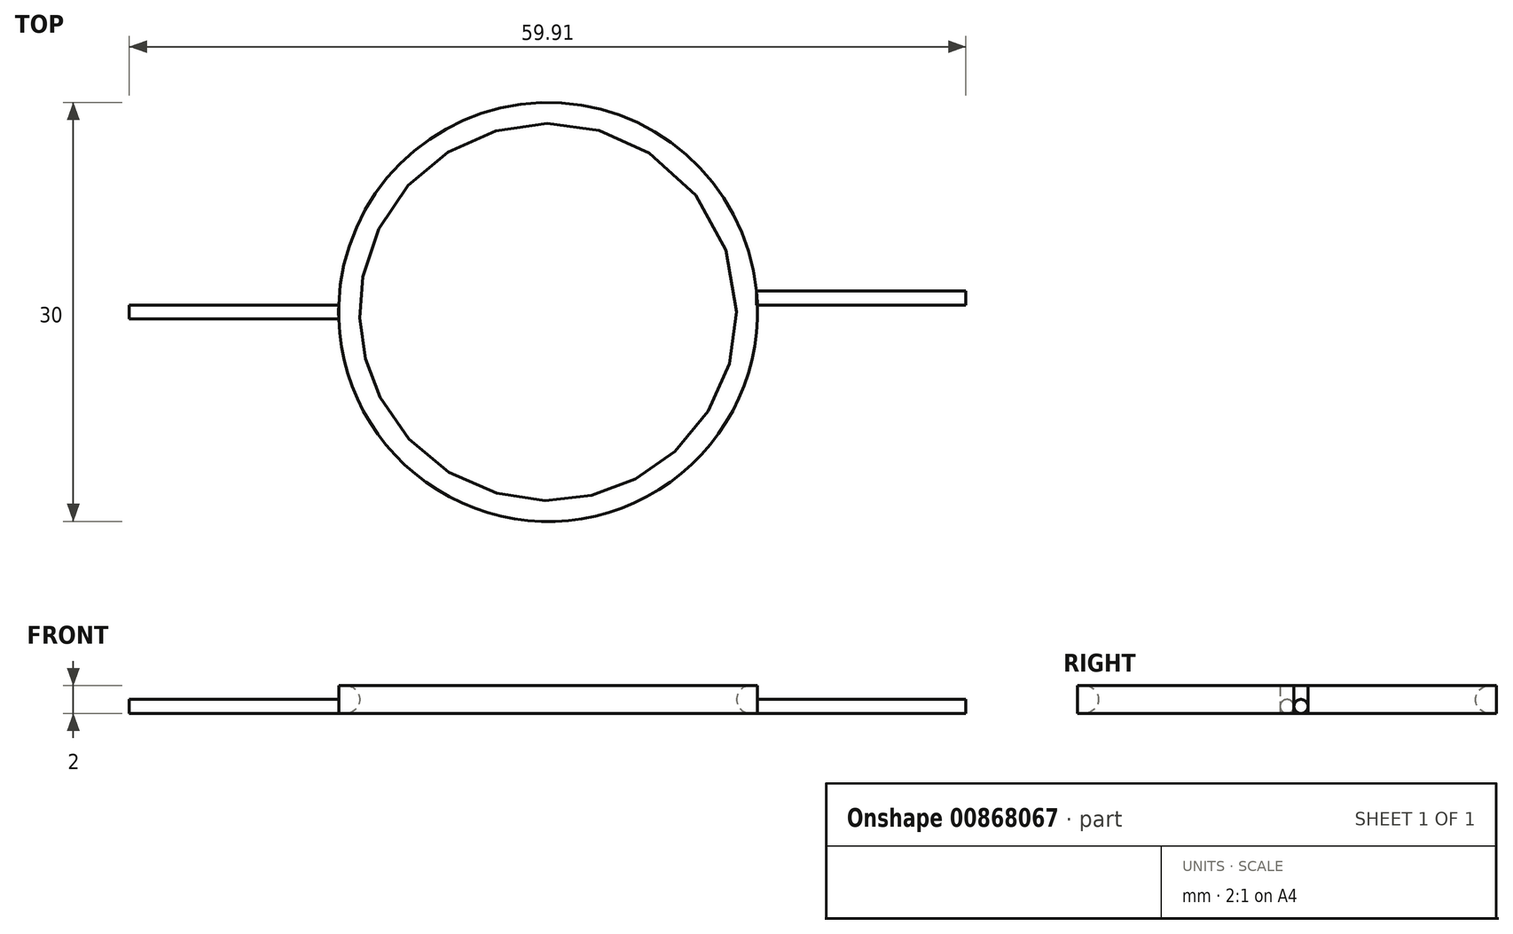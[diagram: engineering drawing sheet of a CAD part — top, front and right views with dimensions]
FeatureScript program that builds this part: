
annotation { "Feature Type Name" : "Feature", "Feature Type Description" : "" }
export const myFeature = defineFeature(function(context is Context, id is Id, definition is map)
    precondition{}
    {
        {
            var Q0;
            Q0=qCreatedBy(makeId("Top.planeOp"),FACE);
            var sketch = newSketch(context, id + "F0", { "sketchPlane" : qUnion([Q0])});
            skCircle(sketch, "E0", {"center": v(0, 0) * mm, "radius": 15 * mm});
            skLineSegment(sketch, "E1.bottom", {"start": v(14.92, 1.5) * mm, "end": v(29.92, 1.5) * mm});
            skLineSegment(sketch, "E1.top", {"start": v(14.92, 0.5) * mm, "end": v(29.92, 0.5) * mm});
            skLineSegment(sketch, "E1.left", {"start": v(14.92, 1.5) * mm, "end": v(14.92, 0.5) * mm});
            skLineSegment(sketch, "E1.right", {"start": v(29.92, 1.5) * mm, "end": v(29.92, 0.5) * mm});
            skLineSegment(sketch, "E2.bottom", {"start": v(-15, 0.5) * mm, "end": v(-30, 0.5) * mm});
            skLineSegment(sketch, "E2.top", {"start": v(-15, -0.5) * mm, "end": v(-30, -0.5) * mm});
            skLineSegment(sketch, "E2.left", {"start": v(-15, 0.5) * mm, "end": v(-15, -0.5) * mm});
            skLineSegment(sketch, "E2.right", {"start": v(-30, 0.5) * mm, "end": v(-30, -0.5) * mm});
            skCircle(sketch, "E3", {"center": v(0, 0) * mm, "radius": 13.5 * mm});
            skSolve(sketch);
        }
        {
            var Q0;
            {var subQ0=sQuery(id+"F0.wireOp",EDGE,"E1.left");Q0=makeQuery(id+"F0.imprint","IMPRINT",FACE,{"disambiguationData":[TD([[makeQuery(id+"F0.imprint","IMPRINT",EDGE,{"derivedFrom":subQ0}),-1.0]])]});}
            extrude(context, id + "F1", {"entities" : qUnion([Q0]), "depth" : 2 * mm, "offsetDistance" : 25 * mm});
        }
        {
            var Q0;
            {var subQ1=sQuery(id+"F0.wireOp",EDGE,"E2.bottom");Q0=makeQuery(id+"F0.imprint","IMPRINT",FACE,{"disambiguationData":[TD([[makeQuery(id+"F0.imprint","IMPRINT",EDGE,{"derivedFrom":subQ1}),1.0]])]});}
            var Q1;
            {var subQ0=sQuery(id+"F0.wireOp",EDGE,"E1.bottom");Q1=makeQuery(id+"F0.imprint","IMPRINT",FACE,{"disambiguationData":[TD([[makeQuery(id+"F0.imprint","IMPRINT",EDGE,{"derivedFrom":subQ0}),-1.0]])]});}
            extrude(context, id + "F2", {"entities" : qUnion([Q0, Q1]), "depth" : 1 * mm, "offsetDistance" : 25 * mm});
        }
        {
            var Q0;
            Q0=makeQuery(id+"F2.opExtrude","CAP_EDGE",EDGE,{"disambiguationData":[OSD([sQuery(id+"F0.wireOp",EDGE,"E2.bottom")])],"isStart":false});
            var Q1;
            Q1=makeQuery(id+"F2.opExtrude","CAP_EDGE",EDGE,{"disambiguationData":[OSD([sQuery(id+"F0.wireOp",EDGE,"E2.top")])],"isStart":false});
            var Q2;
            Q2=makeQuery(id+"F2.opExtrude","CAP_EDGE",EDGE,{"disambiguationData":[OSD([sQuery(id+"F0.wireOp",EDGE,"E2.bottom")])],"isStart":true});
            var Q3;
            Q3=makeQuery(id+"F2.opExtrude","CAP_EDGE",EDGE,{"disambiguationData":[OSD([sQuery(id+"F0.wireOp",EDGE,"E2.top")])],"isStart":true});
            var Q4;
            Q4=makeQuery(id+"F2.opExtrude","CAP_EDGE",EDGE,{"disambiguationData":[OSD([sQuery(id+"F0.wireOp",EDGE,"E1.bottom")])],"isStart":true});
            var Q5;
            Q5=makeQuery(id+"F2.opExtrude","CAP_EDGE",EDGE,{"disambiguationData":[OSD([sQuery(id+"F0.wireOp",EDGE,"E1.top")])],"isStart":true});
            var Q6;
            Q6=makeQuery(id+"F2.opExtrude","CAP_EDGE",EDGE,{"disambiguationData":[OSD([sQuery(id+"F0.wireOp",EDGE,"E1.top")])],"isStart":false});
            var Q7;
            Q7=makeQuery(id+"F2.opExtrude","CAP_EDGE",EDGE,{"disambiguationData":[OSD([sQuery(id+"F0.wireOp",EDGE,"E1.bottom")])],"isStart":false});
            fillet(context, id + "F3", {"entities" : qUnion([Q0, Q1, Q2, Q3, Q4, Q5, Q6, Q7]), "radius" : 0.5 * mm, "tangentPropagation" : true, "allowEdgeOverflow" : false});
        }
        {
            var Q0;
            Q0=makeQuery(id+"F1.opExtrude","CAP_EDGE",EDGE,{"disambiguationData":[OSD([sQuery(id+"F0.wireOp",EDGE,"E3")])],"isStart":false});
            var Q1;
            Q1=makeQuery(id+"F1.opExtrude","CAP_EDGE",EDGE,{"disambiguationData":[OSD([sQuery(id+"F0.wireOp",EDGE,"E3")])],"isStart":true});
            fillet(context, id + "F4", {"entities" : qUnion([Q0, Q1]), "radius" : 1 * mm, "tangentPropagation" : true, "allowEdgeOverflow" : false});
        }
    });
